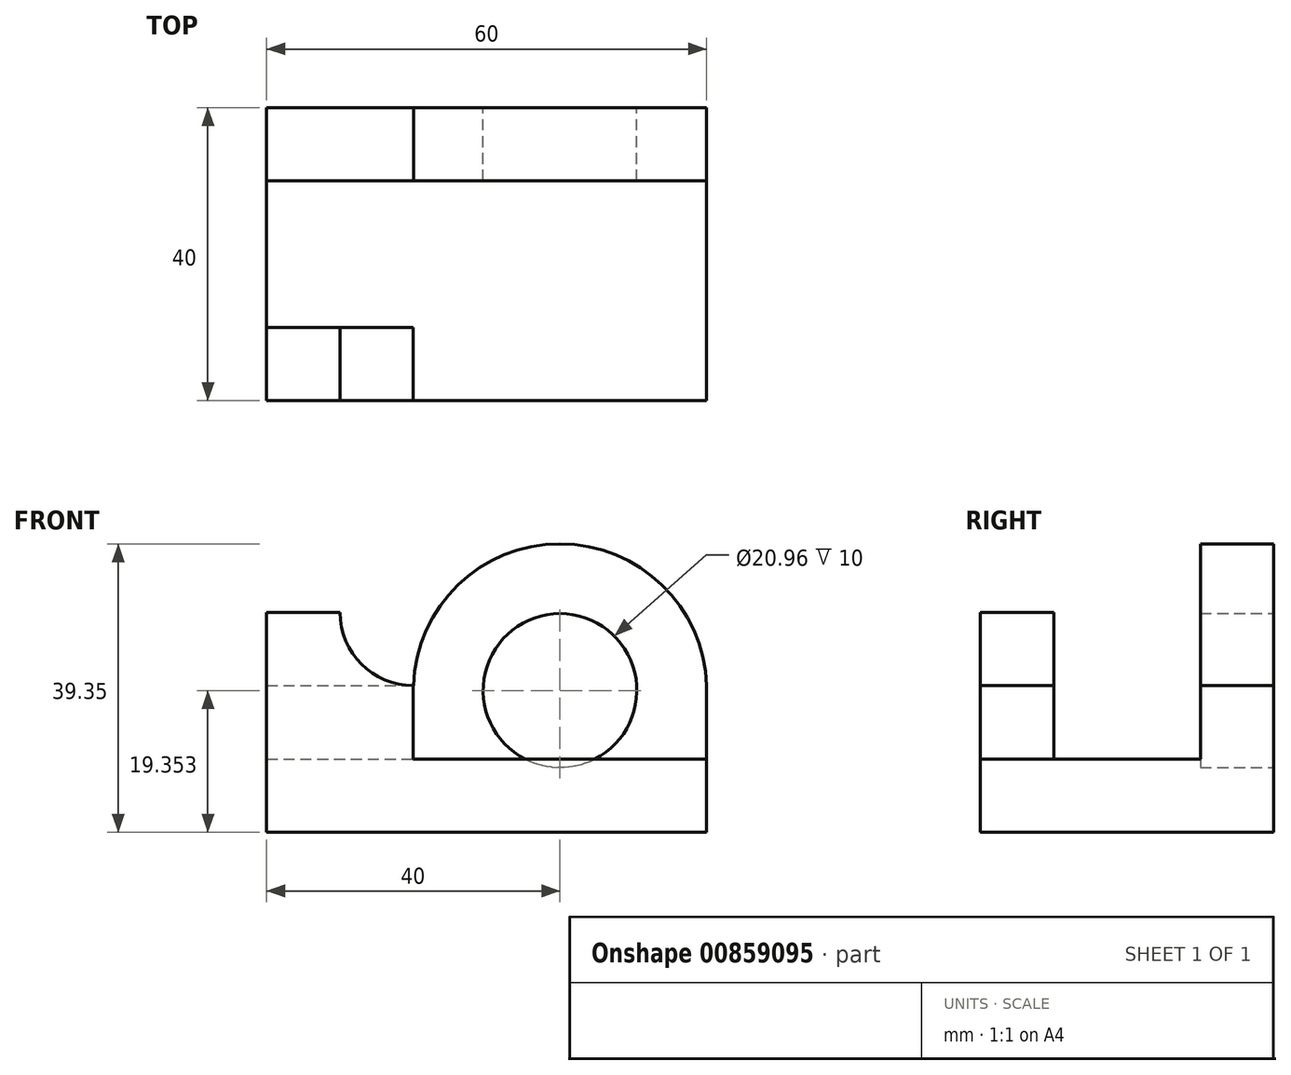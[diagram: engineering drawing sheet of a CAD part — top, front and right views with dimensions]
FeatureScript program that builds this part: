
annotation { "Feature Type Name" : "Feature", "Feature Type Description" : "" }
export const myFeature = defineFeature(function(context is Context, id is Id, definition is map)
    precondition{}
    {
        {
            var Q0;
            Q0=qCreatedBy(makeId("Top.planeOp"),FACE);
            var sketch = newSketch(context, id + "F0", { "sketchPlane" : qUnion([Q0])});
            skLineSegment(sketch, "E0.bottom", {"start": v(0, 0) * mm, "end": v(60, 0) * mm});
            skLineSegment(sketch, "E0.top", {"start": v(0, 40) * mm, "end": v(60, 40) * mm});
            skLineSegment(sketch, "E0.left", {"start": v(0, 0) * mm, "end": v(0, 40) * mm});
            skLineSegment(sketch, "E0.right", {"start": v(60, 0) * mm, "end": v(60, 40) * mm});
            skSolve(sketch);
        }
        {
            var Q0;
            Q0=makeQuery(id+"F0.imprint","IMPRINT",FACE,{"disambiguationData":[TD([[makeQuery(id+"F0.imprint","IMPRINT",EDGE,{"derivedFrom":sQuery(id+"F0.wireOp",EDGE,"E0.bottom")}),1.0]])]});
            extrude(context, id + "F1", {"entities" : qUnion([Q0]), "depth" : 10 * mm, "offsetDistance" : 25 * mm});
        }
        {
            var Q0;
            Q0=makeQuery(id+"F1.opExtrude","CAP_FACE",FACE,{"disambiguationData":[OSD([sQuery(id+"F0.wireOp",EDGE,"E0.bottom"),sQuery(id+"F0.wireOp",EDGE,"E0.top"),sQuery(id+"F0.wireOp",EDGE,"E0.left"),sQuery(id+"F0.wireOp",EDGE,"E0.right")])],"isStart":false});
            var sketch = newSketch(context, id + "F2", { "sketchPlane" : qUnion([Q0])});
            skLineSegment(sketch, "E1.bottom", {"start": v(0, 0) * mm, "end": v(20, 0) * mm});
            skLineSegment(sketch, "E1.top", {"start": v(0, 10) * mm, "end": v(20, 10) * mm});
            skLineSegment(sketch, "E1.left", {"start": v(0, 0) * mm, "end": v(0, 10) * mm});
            skLineSegment(sketch, "E1.right", {"start": v(20, 0) * mm, "end": v(20, 10) * mm});
            skLineSegment(sketch, "E2.bottom", {"start": v(0, 40) * mm, "end": v(60, 40) * mm});
            skLineSegment(sketch, "E2.left", {"start": v(0, 40) * mm, "end": v(0, 30) * mm});
            skLineSegment(sketch, "E2.right", {"start": v(60, 40) * mm, "end": v(60, 30) * mm});
            skLineSegment(sketch, "E3.bottom", {"start": v(0, 30) * mm, "end": v(20, 30) * mm});
            skLineSegment(sketch, "E3.top", {"start": v(0, 40) * mm, "end": v(20, 40) * mm});
            skLineSegment(sketch, "E3.left", {"start": v(0, 30) * mm, "end": v(0, 40) * mm});
            skLineSegment(sketch, "E3.right", {"start": v(20, 30) * mm, "end": v(20, 40) * mm});
            skLineSegment(sketch, "E4.bottom", {"start": v(60, 30) * mm, "end": v(40, 30) * mm});
            skLineSegment(sketch, "E4.top", {"start": v(60, 40) * mm, "end": v(40, 40) * mm});
            skLineSegment(sketch, "E4.left", {"start": v(60, 30) * mm, "end": v(60, 40) * mm});
            skLineSegment(sketch, "E4.right", {"start": v(40, 30) * mm, "end": v(40, 40) * mm});
            skLineSegment(sketch, "E5", {"start": v(20, 30) * mm, "end": v(40, 30) * mm});
            skSolve(sketch);
        }
        {
            var Q0;
            Q0=makeQuery(id+"F2.imprint","IMPRINT",FACE,{"disambiguationData":[TD([[makeQuery(id+"F2.imprint","IMPRINT",EDGE,{"derivedFrom":sQuery(id+"F2.wireOp",EDGE,"E1.bottom")}),1.0]])]});
            var Q1;
            Q1=makeQuery(id+"F2.imprint","IMPRINT",FACE,{"disambiguationData":[TD([[makeQuery(id+"F2.imprint","IMPRINT",EDGE,{"derivedFrom":sQuery(id+"F2.wireOp",EDGE,"E3.bottom")}),1.0]])]});
            var Q2;
            Q2=makeQuery(id+"F2.imprint","IMPRINT",FACE,{"disambiguationData":[TD([[makeQuery(id+"F2.imprint","IMPRINT",EDGE,{"derivedFrom":sQuery(id+"F2.wireOp",EDGE,"E4.bottom")}),-1.0]])]});
            var Q3;
            Q3=makeQuery(id+"F2.imprint","IMPRINT",FACE,{"disambiguationData":[TD([[makeQuery(id+"F2.imprint","IMPRINT",EDGE,{"derivedFrom":sQuery(id+"F2.wireOp",EDGE,"E2.bottom")}),-1.0]])]});
            extrude(context, id + "F3", {"entities" : qUnion([Q0, Q1, Q2, Q3]), "operationType" : NewBodyOperationType.ADD, "depth" : 10 * mm, "offsetDistance" : 25 * mm});
        }
        {
            var Q0;
            {var subQ0=sQuery(id+"F2.wireOp",EDGE,"E4.top");var subQ1=sQuery(id+"F2.wireOp",EDGE,"E3.top");var subQ2=sQuery(id+"F2.wireOp",EDGE,"E2.bottom");Q0=makeQuery(id+"FJLtRiwC5AthFLY_1.boolean.opBoolean","MERGE",FACE,{"derivedFrom":[makeQuery(id+"F3.boolean.opBoolean","MERGE",FACE,{"derivedFrom":[makeQuery(id+"F1.opExtrude","SWEPT_FACE",FACE,{"disambiguationData":[OSD([sQuery(id+"F0.wireOp",EDGE,"E0.top")])]}),makeQuery(id+"F3.opExtrude","SWEPT_FACE",FACE,{"disambiguationData":[OSD([subQ2,subQ1,subQ0])]})]}),makeQuery(id+"FJLtRiwC5AthFLY_1.opExtrude","SWEPT_FACE",FACE,{"disambiguationData":[OSD([subQ2,subQ1,subQ0])]})]});}
            var sketch = newSketch(context, id + "F4", { "sketchPlane" : qUnion([Q0])});
            skCircle(sketch, "E6", {"center": v(-40, 19.35) * mm, "radius": 20 * mm});
            skLineSegment(sketch, "E7", {"start": v(-20, 30) * mm, "end": v(-20, 8.34) * mm});
            skCircle(sketch, "E8", {"center": v(-40, 19.35) * mm, "radius": 10.48 * mm});
            skSolve(sketch);
        }
        {
            var Q0;
            Q0=makeQuery(id+"F4.imprint","IMPRINT",FACE,{"disambiguationData":[TD([[makeQuery(id+"F4.imprint","IMPRINT",EDGE,{"derivedFrom":sQuery(id+"F4.wireOp",EDGE,"E8")}),-1.0]])]});
            var Q1;
            {var subQ0=sQuery(id+"F4.wireOp",EDGE,"E6");var subQ1=makeQuery(id+"FJLtRiwC5AthFLY_1.opExtrude","CAP_EDGE",EDGE,{"disambiguationData":[OSD([sQuery(id+"F2.wireOp",EDGE,"E2.bottom"),sQuery(id+"F2.wireOp",EDGE,"E3.top"),sQuery(id+"F2.wireOp",EDGE,"E4.top")])],"isStart":false});var subQ2=makeQuery(id+"F4.imprint","INTERSECT",VERTEX,{"disambiguationData":[OD(0.0)],"derivedFrom":[subQ1,subQ0]});Q1=makeQuery(id+"F4.imprint","IMPRINT",FACE,{"disambiguationData":[TD([[makeQuery(id+"F4.imprint","IMPRINT",EDGE,{"disambiguationData":[TD([[subQ2,-1.0]])],"derivedFrom":subQ0}),1.0]])]});}
            extrude(context, id + "F5", {"entities" : qUnion([Q0, Q1]), "operationType" : NewBodyOperationType.ADD, "oppositeDirection" : true, "depth" : 10 * mm, "offsetDistance" : 25 * mm});
        }
        {
            var Q0;
            Q0=makeQuery(id+"F4.imprint","IMPRINT",FACE,{"disambiguationData":[TD([[makeQuery(id+"F4.imprint","IMPRINT",EDGE,{"derivedFrom":sQuery(id+"F4.wireOp",EDGE,"E8")}),1.0]])]});
            extrude(context, id + "F6", {"entities" : qUnion([Q0]), "operationType" : NewBodyOperationType.REMOVE, "oppositeDirection" : true, "depth" : 10 * mm, "offsetDistance" : 25 * mm});
        }
        {
            var Q0;
            Q0=makeQuery(id+"F3.opExtrude","CAP_FACE",FACE,{"disambiguationData":[OSD([sQuery(id+"F2.wireOp",EDGE,"E1.bottom"),sQuery(id+"F2.wireOp",EDGE,"E1.top"),sQuery(id+"F2.wireOp",EDGE,"E1.left"),sQuery(id+"F2.wireOp",EDGE,"E1.right")])],"isStart":false});
            extrude(context, id + "F7", {"entities" : qUnion([Q0]), "operationType" : NewBodyOperationType.ADD, "depth" : 10 * mm, "offsetDistance" : 25 * mm});
        }
        {
            var Q0;
            {var subQ0=sQuery(id+"F2.wireOp",EDGE,"E1.bottom");Q0=makeQuery(id+"F7.boolean.opBoolean","MERGE",FACE,{"derivedFrom":[makeQuery(id+"F3.boolean.opBoolean","MERGE",FACE,{"derivedFrom":[makeQuery(id+"F1.opExtrude","SWEPT_FACE",FACE,{"disambiguationData":[OSD([sQuery(id+"F0.wireOp",EDGE,"E0.bottom")])]}),makeQuery(id+"F3.opExtrude","SWEPT_FACE",FACE,{"disambiguationData":[OSD([subQ0])]})]}),makeQuery(id+"F7.opExtrude","SWEPT_FACE",FACE,{"disambiguationData":[OSD([subQ0])]})]});}
            var sketch = newSketch(context, id + "F8", { "sketchPlane" : qUnion([Q0])});
            skArc(sketch, "E9", {"start": v(10, 30) * mm, "mid": v(12.93, 22.93) * mm, "end": v(20, 20) * mm});
            skLineSegment(sketch, "E10", {"start": v(10, 30) * mm, "end": v(20, 30) * mm});
            skLineSegment(sketch, "E11", {"start": v(0, 30) * mm, "end": v(10, 30) * mm});
            skSolve(sketch);
        }
        {
            var Q0;
            {var subQ0=sQuery(id+"F8.wireOp",EDGE,"E9");Q0=makeQuery(id+"F8.imprint","IMPRINT",FACE,{"disambiguationData":[TD([[makeQuery(id+"F8.imprint","IMPRINT",EDGE,{"derivedFrom":subQ0}),1.0]])]});}
            extrude(context, id + "F9", {"entities" : qUnion([Q0]), "operationType" : NewBodyOperationType.REMOVE, "oppositeDirection" : true, "depth" : 10 * mm, "offsetDistance" : 25 * mm});
        }
    });
